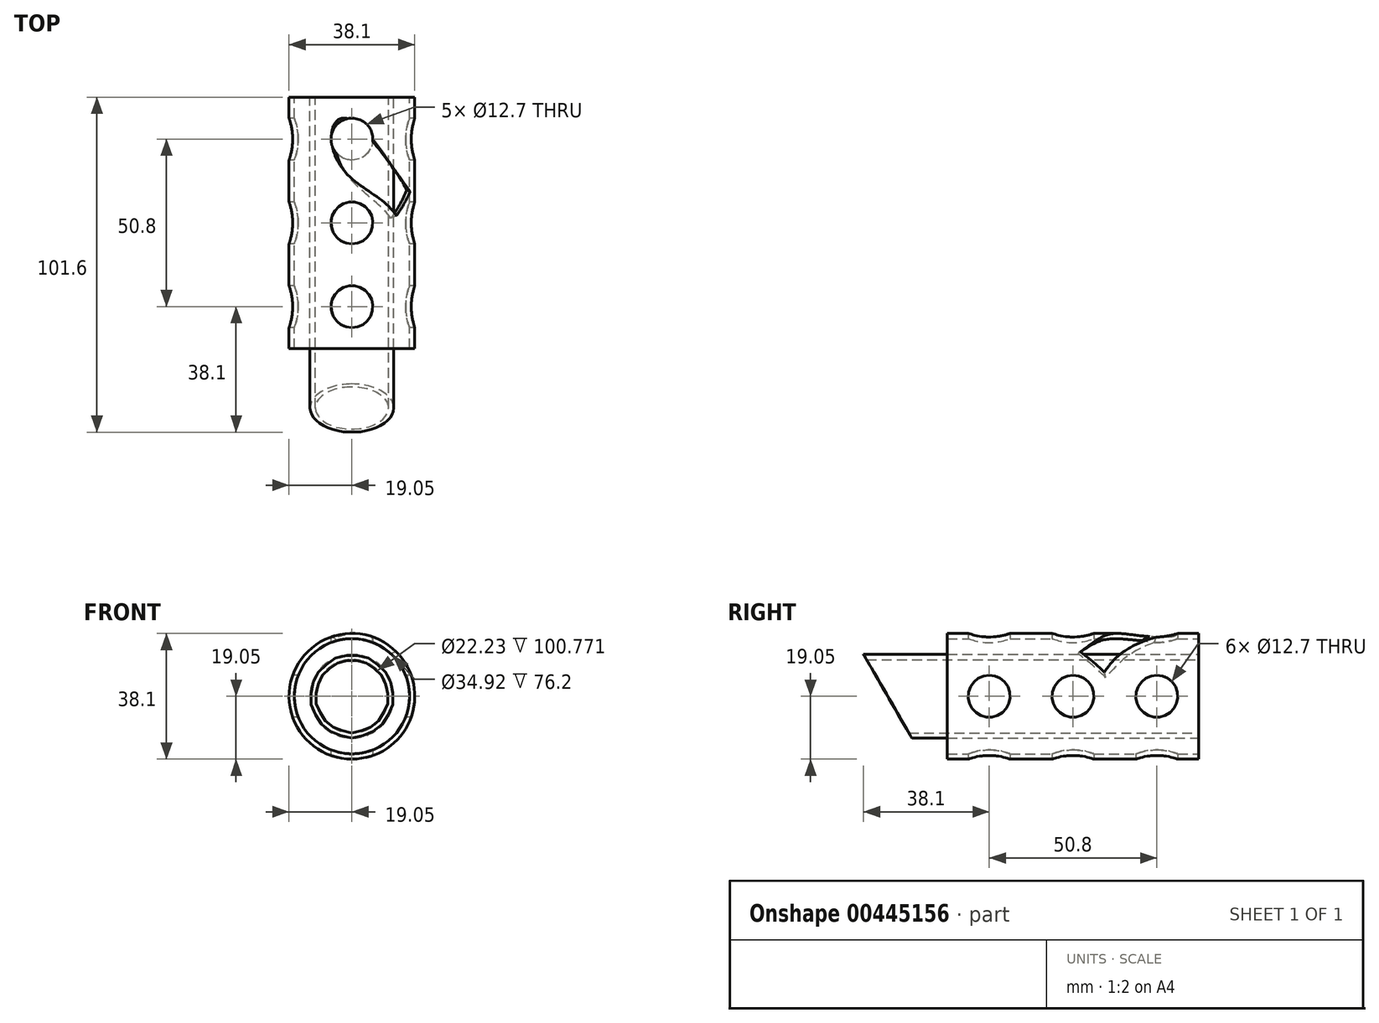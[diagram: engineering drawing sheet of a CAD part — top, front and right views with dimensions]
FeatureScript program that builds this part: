
annotation { "Feature Type Name" : "Feature", "Feature Type Description" : "" }
export const myFeature = defineFeature(function(context is Context, id is Id, definition is map)
    precondition{}
    {
        {
            var Q0;
            Q0=qCreatedBy(makeId("Front.planeOp"),FACE);
            var sketch = newSketch(context, id + "F0", { "sketchPlane" : qUnion([Q0])});
            skCircle(sketch, "E0", {"center": v(0, 0) * mm, "radius": 19.05 * mm});
            skCircle(sketch, "E1", {"center": v(0, 0) * mm, "radius": 17.46 * mm});
            skCircle(sketch, "E2", {"center": v(0, 0) * mm, "radius": 11.11 * mm});
            skCircle(sketch, "E3", {"center": v(0, 0) * mm, "radius": 12.7 * mm});
            skSolve(sketch);
        }
        {
            var Q0;
            Q0=makeQuery(id+"F0.imprint","IMPRINT",FACE,{"disambiguationData":[TD([[makeQuery(id+"F0.imprint","IMPRINT",EDGE,{"derivedFrom":sQuery(id+"F0.wireOp",EDGE,"E0")}),1.0]])]});
            extrude(context, id + "F1", {"entities" : qUnion([Q0]), "depth" : 76.2 * mm});
        }
        {
            var Q0;
            Q0=qCreatedBy(makeId("Right.planeOp"),FACE);
            var sketch = newSketch(context, id + "F2", { "sketchPlane" : qUnion([Q0])});
            skLineSegment(sketch, "E4", {"start": v(0, 0) * mm, "end": v(-12.7, 0) * mm});
            skCircle(sketch, "E5", {"center": v(-12.7, 0) * mm, "radius": 6.35 * mm});
            skLineSegment(sketch, "E6", {"start": v(-12.7, 0) * mm, "end": v(-38.1, 0) * mm});
            skCircle(sketch, "E7", {"center": v(-38.1, 0) * mm, "radius": 6.35 * mm});
            skLineSegment(sketch, "E8", {"start": v(-38.1, 0) * mm, "end": v(-63.5, 0) * mm});
            skCircle(sketch, "E9", {"center": v(-63.5, 0) * mm, "radius": 6.35 * mm});
            skSolve(sketch);
        }
        {
            var Q0;
            Q0=qCreatedBy(makeId("Top.planeOp"),FACE);
            var Q1;
            Q1=sQuery(id+"F2.wireOp",EDGE,"E8");
            cPlane(context, id + "F3", {"entities" : qUnion([Q0, Q1]), "cplaneType" : CPlaneType.LINE_ANGLE, "offset" : 25.4 * mm, "angle" : 45 * degree, "width" : 152.4 * mm, "height" : 152.4 * mm});
        }
        {
            var Q0;
            Q0=qCreatedBy(id+"F3.planeOp",FACE);
            var sketch = newSketch(context, id + "F4", { "sketchPlane" : qUnion([Q0])});
            skLineSegment(sketch, "E10.0", {"start": v(0, 38.1) * mm, "end": v(0, 63.5) * mm});
            skPoint(sketch, "E11.0", {"position": v(0, 12.7) * mm});
            skLineSegment(sketch, "E12", {"start": v(0, 38.1) * mm, "end": v(0, 12.7) * mm});
            skCircle(sketch, "E13", {"center": v(0, 25.4) * mm, "radius": 6.35 * mm});
            skCircle(sketch, "E14", {"center": v(0, 50.8) * mm, "radius": 6.35 * mm});
            skSolve(sketch);
        }
        {
            var Q0;
            Q0=qCreatedBy(makeId("Top.planeOp"),FACE);
            var Q1;
            Q1=sQuery(id+"F4.wireOp",EDGE,"E10.0");
            cPlane(context, id + "F5", {"entities" : qUnion([Q0, Q1]), "cplaneType" : CPlaneType.LINE_ANGLE, "offset" : 25.4 * mm, "angle" : 45 * degree, "oppositeDirection" : true, "width" : 152.4 * mm, "height" : 152.4 * mm});
        }
        {
            var Q0;
            Q0=qCreatedBy(id+"F5.planeOp",FACE);
            var sketch = newSketch(context, id + "F6", { "sketchPlane" : qUnion([Q0])});
            skLineSegment(sketch, "E15.0", {"start": v(0, 38.1) * mm, "end": v(0, 63.5) * mm});
            skLineSegment(sketch, "E16.0", {"start": v(0, 12.7) * mm, "end": v(0, 38.1) * mm});
            skCircle(sketch, "E17", {"center": v(0, 25.4) * mm, "radius": 6.35 * mm});
            skCircle(sketch, "E18", {"center": v(0, 50.8) * mm, "radius": 6.35 * mm});
            skSolve(sketch);
        }
        {
            var Q0;
            {var subQ0=sQuery(id+"F4.wireOp",EDGE,"E14");var subQ1=sQuery(id+"F4.wireOp",EDGE,"E10.0");var subQ2=makeQuery(id+"F4.imprint","INTERSECT",VERTEX,{"disambiguationData":[OD(0.0)],"derivedFrom":[subQ1,subQ0]});Q0=makeQuery(id+"F4.imprint","IMPRINT",FACE,{"disambiguationData":[TD([[makeQuery(id+"F4.imprint","IMPRINT",EDGE,{"disambiguationData":[TD([[subQ2,1.0]])],"derivedFrom":subQ1}),-1.0]])]});}
            var Q1;
            {var subQ0=sQuery(id+"F4.wireOp",EDGE,"E14");var subQ1=sQuery(id+"F4.wireOp",EDGE,"E10.0");var subQ2=makeQuery(id+"F4.imprint","INTERSECT",VERTEX,{"disambiguationData":[OD(0.0)],"derivedFrom":[subQ1,subQ0]});Q1=makeQuery(id+"F4.imprint","IMPRINT",FACE,{"disambiguationData":[TD([[makeQuery(id+"F4.imprint","IMPRINT",EDGE,{"disambiguationData":[TD([[subQ2,1.0]])],"derivedFrom":subQ1}),1.0]])]});}
            var Q2;
            {var subQ0=sQuery(id+"F4.wireOp",EDGE,"E13");var subQ1=sQuery(id+"F4.wireOp",EDGE,"E12");var subQ2=makeQuery(id+"F4.imprint","INTERSECT",VERTEX,{"disambiguationData":[OD(0.0)],"derivedFrom":[subQ1,subQ0]});Q2=makeQuery(id+"F4.imprint","IMPRINT",FACE,{"disambiguationData":[TD([[makeQuery(id+"F4.imprint","IMPRINT",EDGE,{"disambiguationData":[TD([[subQ2,-1.0]])],"derivedFrom":subQ1}),-1.0]])]});}
            var Q3;
            {var subQ0=sQuery(id+"F4.wireOp",EDGE,"E13");var subQ1=sQuery(id+"F4.wireOp",EDGE,"E12");var subQ2=makeQuery(id+"F4.imprint","INTERSECT",VERTEX,{"disambiguationData":[OD(0.0)],"derivedFrom":[subQ1,subQ0]});Q3=makeQuery(id+"F4.imprint","IMPRINT",FACE,{"disambiguationData":[TD([[makeQuery(id+"F4.imprint","IMPRINT",EDGE,{"disambiguationData":[TD([[subQ2,-1.0]])],"derivedFrom":subQ1}),1.0]])]});}
            extrude(context, id + "F7", {"entities" : qUnion([Q0, Q1, Q2, Q3]), "operationType" : NewBodyOperationType.REMOVE, "endBound" : BoundingType.SYMMETRIC, "oppositeDirection" : true, "depth" : 50.8 * mm});
        }
        {
            var Q0;
            Q0=makeQuery(id+"F2.imprint","IMPRINT",FACE,{"disambiguationData":[TD([[makeQuery(id+"F2.imprint","IMPRINT",EDGE,{"derivedFrom":sQuery(id+"F2.wireOp",EDGE,"E9")}),1.0]])]});
            var Q1;
            {var subQ0=sQuery(id+"F2.wireOp",EDGE,"E8");var subQ1=sQuery(id+"F2.wireOp",EDGE,"E6");var subQ2=makeQuery(id+"F2.imprint","INTERSECT",VERTEX,{"derivedFrom":[subQ1,subQ0]});Q1=makeQuery(id+"F2.imprint","IMPRINT",FACE,{"disambiguationData":[TD([[makeQuery(id+"F2.imprint","IMPRINT",EDGE,{"disambiguationData":[TD([[subQ2,1.0]])],"derivedFrom":subQ1}),-1.0]])]});}
            var Q2;
            {var subQ0=sQuery(id+"F2.wireOp",EDGE,"E6");var subQ1=sQuery(id+"F2.wireOp",EDGE,"E4");var subQ2=makeQuery(id+"F2.imprint","INTERSECT",VERTEX,{"derivedFrom":[subQ1,subQ0]});Q2=makeQuery(id+"F2.imprint","IMPRINT",FACE,{"disambiguationData":[TD([[makeQuery(id+"F2.imprint","IMPRINT",EDGE,{"disambiguationData":[TD([[subQ2,1.0]])],"derivedFrom":subQ1}),-1.0]])]});}
            var Q3;
            {var subQ0=sQuery(id+"F2.wireOp",EDGE,"E8");var subQ1=sQuery(id+"F2.wireOp",EDGE,"E6");var subQ2=makeQuery(id+"F2.imprint","INTERSECT",VERTEX,{"derivedFrom":[subQ1,subQ0]});Q3=makeQuery(id+"F2.imprint","IMPRINT",FACE,{"disambiguationData":[TD([[makeQuery(id+"F2.imprint","IMPRINT",EDGE,{"disambiguationData":[TD([[subQ2,1.0]])],"derivedFrom":subQ1}),1.0]])]});}
            var Q4;
            {var subQ0=sQuery(id+"F2.wireOp",EDGE,"E6");var subQ1=sQuery(id+"F2.wireOp",EDGE,"E4");var subQ2=makeQuery(id+"F2.imprint","INTERSECT",VERTEX,{"derivedFrom":[subQ1,subQ0]});Q4=makeQuery(id+"F2.imprint","IMPRINT",FACE,{"disambiguationData":[TD([[makeQuery(id+"F2.imprint","IMPRINT",EDGE,{"disambiguationData":[TD([[subQ2,1.0]])],"derivedFrom":subQ1}),1.0]])]});}
            extrude(context, id + "F8", {"entities" : qUnion([Q0, Q1, Q2, Q3, Q4]), "operationType" : NewBodyOperationType.REMOVE, "endBound" : BoundingType.SYMMETRIC, "depth" : 50.8 * mm});
        }
        {
            var Q0;
            {var subQ0=sQuery(id+"F6.wireOp",EDGE,"E18");var subQ1=sQuery(id+"F6.wireOp",EDGE,"E15.0");var subQ2=makeQuery(id+"F6.imprint","INTERSECT",VERTEX,{"disambiguationData":[OD(0.0)],"derivedFrom":[subQ1,subQ0]});Q0=makeQuery(id+"F6.imprint","IMPRINT",FACE,{"disambiguationData":[TD([[makeQuery(id+"F6.imprint","IMPRINT",EDGE,{"disambiguationData":[TD([[subQ2,1.0]])],"derivedFrom":subQ1}),1.0]])]});}
            var Q1;
            {var subQ0=sQuery(id+"F6.wireOp",EDGE,"E18");var subQ1=sQuery(id+"F6.wireOp",EDGE,"E15.0");var subQ2=makeQuery(id+"F6.imprint","INTERSECT",VERTEX,{"disambiguationData":[OD(0.0)],"derivedFrom":[subQ1,subQ0]});Q1=makeQuery(id+"F6.imprint","IMPRINT",FACE,{"disambiguationData":[TD([[makeQuery(id+"F6.imprint","IMPRINT",EDGE,{"disambiguationData":[TD([[subQ2,1.0]])],"derivedFrom":subQ1}),-1.0]])]});}
            var Q2;
            {var subQ0=sQuery(id+"F6.wireOp",EDGE,"E17");var subQ1=sQuery(id+"F6.wireOp",EDGE,"E16.0");var subQ2=makeQuery(id+"F6.imprint","INTERSECT",VERTEX,{"disambiguationData":[OD(0.0)],"derivedFrom":[subQ1,subQ0]});Q2=makeQuery(id+"F6.imprint","IMPRINT",FACE,{"disambiguationData":[TD([[makeQuery(id+"F6.imprint","IMPRINT",EDGE,{"disambiguationData":[TD([[subQ2,1.0]])],"derivedFrom":subQ1}),-1.0]])]});}
            var Q3;
            {var subQ0=sQuery(id+"F6.wireOp",EDGE,"E17");var subQ1=sQuery(id+"F6.wireOp",EDGE,"E16.0");var subQ2=makeQuery(id+"F6.imprint","INTERSECT",VERTEX,{"disambiguationData":[OD(0.0)],"derivedFrom":[subQ1,subQ0]});Q3=makeQuery(id+"F6.imprint","IMPRINT",FACE,{"disambiguationData":[TD([[makeQuery(id+"F6.imprint","IMPRINT",EDGE,{"disambiguationData":[TD([[subQ2,1.0]])],"derivedFrom":subQ1}),1.0]])]});}
            extrude(context, id + "F9", {"entities" : qUnion([Q0, Q1, Q2, Q3]), "operationType" : NewBodyOperationType.REMOVE, "endBound" : BoundingType.SYMMETRIC, "oppositeDirection" : true, "depth" : 50.8 * mm});
        }
        {
            var Q0;
            Q0=qCreatedBy(makeId("Top.planeOp"),FACE);
            var sketch = newSketch(context, id + "F10", { "sketchPlane" : qUnion([Q0])});
            skFitSpline(sketch, "E19.0", {"points": [v(-19.05, -19.05) * mm, v(-19.05, -19.05) * mm, v(-19.02, -18.97) * mm, v(-18.92, -18.66) * mm, v(-18.81, -18.3) * mm, v(-18.72, -17.98) * mm, v(-18.62, -17.6) * mm, v(-18.51, -17.2) * mm, v(-18.4, -16.73) * mm, v(-18.27, -16.06) * mm, v(-18.15, -15.34) * mm, v(-18.05, -14.55) * mm, v(-18, -13.94) * mm, v(-17.97, -13.33) * mm, v(-17.96, -12.7) * mm, v(-17.97, -12.07) * mm, v(-18, -11.45) * mm, v(-18.05, -10.85) * mm, v(-18.15, -10.06) * mm, v(-18.27, -9.33) * mm, v(-18.4, -8.66) * mm, v(-18.51, -8.2) * mm, v(-18.62, -7.8) * mm, v(-18.72, -7.42) * mm, v(-18.81, -7.1) * mm, v(-18.92, -6.74) * mm, v(-19.02, -6.43) * mm, v(-19.05, -6.35) * mm, v(-19.05, -6.35) * mm]});
            skFitSpline(sketch, "E20.0", {"points": [v(19.05, -6.35) * mm, v(19.05, -6.35) * mm, v(19.02, -6.43) * mm, v(18.92, -6.74) * mm, v(18.81, -7.1) * mm, v(18.72, -7.42) * mm, v(18.62, -7.8) * mm, v(18.51, -8.2) * mm, v(18.4, -8.67) * mm, v(18.27, -9.34) * mm, v(18.15, -10.06) * mm, v(18.05, -10.85) * mm, v(18, -11.46) * mm, v(17.97, -12.07) * mm, v(17.96, -12.7) * mm, v(17.97, -13.33) * mm, v(18, -13.95) * mm, v(18.05, -14.55) * mm, v(18.15, -15.34) * mm, v(18.27, -16.07) * mm, v(18.4, -16.74) * mm, v(18.51, -17.2) * mm, v(18.62, -17.6) * mm, v(18.72, -17.98) * mm, v(18.81, -18.3) * mm, v(18.92, -18.66) * mm, v(19.02, -18.97) * mm, v(19.05, -19.05) * mm, v(19.05, -19.05) * mm]});
            skLineSegment(sketch, "E21", {"start": v(0, 0) * mm, "end": v(0, -12.7) * mm});
            skCircle(sketch, "E22", {"center": v(0, -12.7) * mm, "radius": 6.35 * mm});
            skCircle(sketch, "E23.0.1.0", {"center": v(0, -38.1) * mm, "radius": 6.35 * mm});
            skCircle(sketch, "E23.0.2.0", {"center": v(0, -63.5) * mm, "radius": 6.35 * mm});
            skLineSegment(sketch, "E23.direction1", {"start": v(0, -12.7) * mm, "end": v(0, -12.7) * mm});
            skLineSegment(sketch, "E23.direction2", {"start": v(0, -12.7) * mm, "end": v(0, -38.1) * mm, "construction": true});
            skSolve(sketch);
        }
        {
            var Q0;
            Q0=makeQuery(id+"F10.imprint","IMPRINT",FACE,{"disambiguationData":[TD([[makeQuery(id+"F10.imprint","IMPRINT",EDGE,{"derivedFrom":sQuery(id+"F10.wireOp",EDGE,"E22")}),1.0]])]});
            var Q1;
            Q1=makeQuery(id+"F10.imprint","IMPRINT",FACE,{"disambiguationData":[TD([[makeQuery(id+"F10.imprint","IMPRINT",EDGE,{"derivedFrom":sQuery(id+"F10.wireOp",EDGE,"E23.0.1.0")}),1.0]])]});
            var Q2;
            Q2=makeQuery(id+"F10.imprint","IMPRINT",FACE,{"disambiguationData":[TD([[makeQuery(id+"F10.imprint","IMPRINT",EDGE,{"derivedFrom":sQuery(id+"F10.wireOp",EDGE,"E23.0.2.0")}),1.0]])]});
            extrude(context, id + "F11", {"entities" : qUnion([Q0, Q1, Q2]), "operationType" : NewBodyOperationType.REMOVE, "endBound" : BoundingType.SYMMETRIC, "depth" : 50.8 * mm});
        }
        {
            var Q0;
            Q0=makeQuery(id+"F0.imprint","IMPRINT",FACE,{"disambiguationData":[TD([[makeQuery(id+"F0.imprint","IMPRINT",EDGE,{"derivedFrom":sQuery(id+"F0.wireOp",EDGE,"E2")}),-1.0]])]});
            extrude(context, id + "F12", {"entities" : qUnion([Q0]), "depth" : 101.6 * mm});
        }
        {
            var Q0;
            Q0=qCreatedBy(makeId("Right.planeOp"),FACE);
            var sketch = newSketch(context, id + "F13", { "sketchPlane" : qUnion([Q0])});
            skLineSegment(sketch, "E24.0", {"start": v(-101.6, -12.7) * mm, "end": v(-101.6, 12.7) * mm});
            skLineSegment(sketch, "E25", {"start": v(0, -12.7) * mm, "end": v(-101.6, -12.7) * mm});
            skLineSegment(sketch, "E26", {"start": v(-101.6, 12.7) * mm, "end": v(-86.94, -12.7) * mm});
            skSolve(sketch);
        }
        {
            var Q0;
            {var subQ0=sQuery(id+"F13.wireOp",EDGE,"E24.0");Q0=makeQuery(id+"F13.imprint","IMPRINT",FACE,{"disambiguationData":[TD([[makeQuery(id+"F13.imprint","IMPRINT",EDGE,{"derivedFrom":subQ0}),-1.0]])]});}
            extrude(context, id + "F14", {"entities" : qUnion([Q0]), "operationType" : NewBodyOperationType.REMOVE, "endBound" : BoundingType.SYMMETRIC, "depth" : 25.4 * mm});
        }
    });
